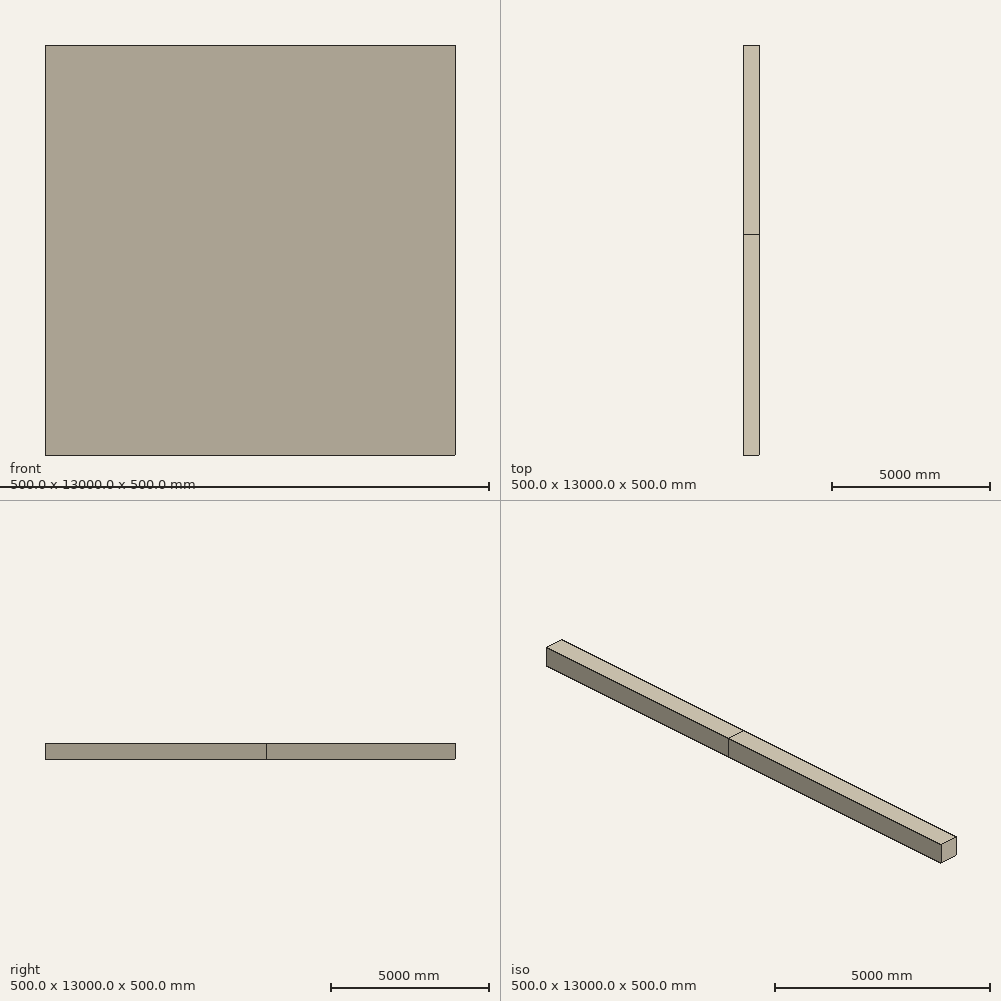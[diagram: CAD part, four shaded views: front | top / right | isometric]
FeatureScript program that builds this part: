
annotation { "Feature Type Name" : "Feature", "Feature Type Description" : "" }
export const myFeature = defineFeature(function(context is Context, id is Id, definition is map)
    precondition{}
    {
        {
            var Q0;
            Q0=qCreatedBy(makeId("Front.planeOp"),FACE);
            var sketch = newSketch(context, id + "F0", { "sketchPlane" : qUnion([Q0])});
            skLineSegment(sketch, "E0.bottom", {"start": v(250, 250) * mm, "end": v(-250, 250) * mm});
            skLineSegment(sketch, "E0.top", {"start": v(250, -250) * mm, "end": v(-250, -250) * mm});
            skLineSegment(sketch, "E0.left", {"start": v(250, 250) * mm, "end": v(250, -250) * mm});
            skLineSegment(sketch, "E0.right", {"start": v(-250, 250) * mm, "end": v(-250, -250) * mm});
            skPoint(sketch, "E0.middle", {"position": v(0, 0) * mm});
            skSolve(sketch);
        }
        {
            var Q0;
            Q0 = qSketchRegion(id + "F0", true);
            extrude(context, id + "F1", {"entities" : qUnion([Q0]), "depth" : 6000 * mm, "offsetDistance" : 25.4 * mm});
        }
        {
            var Q0;
            Q0=makeQuery(id+"F1.opExtrude","CAP_FACE",FACE,{"disambiguationData":[OSD([sQuery(id+"F0.wireOp",EDGE,"E0.bottom"),sQuery(id+"F0.wireOp",EDGE,"E0.top"),sQuery(id+"F0.wireOp",EDGE,"E0.left"),sQuery(id+"F0.wireOp",EDGE,"E0.right")])],"isStart":false});
            extrude(context, id + "F2", {"entities" : qUnion([Q0]), "depth" : 7000 * mm, "offsetDistance" : 25.4 * mm});
        }
    });
